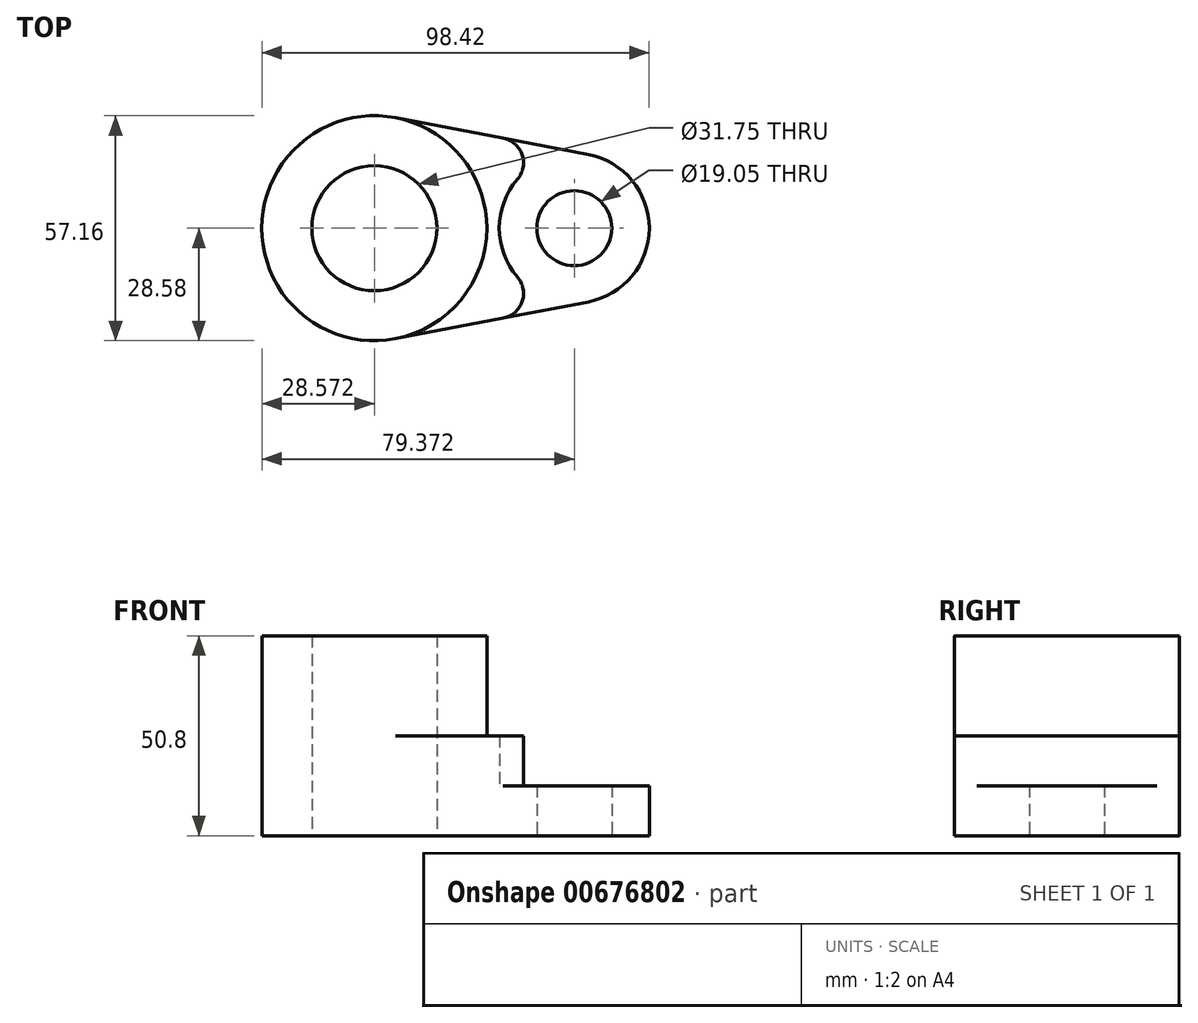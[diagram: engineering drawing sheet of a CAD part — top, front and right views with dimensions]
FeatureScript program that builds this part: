
annotation { "Feature Type Name" : "Feature", "Feature Type Description" : "" }
export const myFeature = defineFeature(function(context is Context, id is Id, definition is map)
    precondition{}
    {
        {
            var Q0;
            Q0=qCreatedBy(makeId("Top.planeOp"),FACE);
            var sketch = newSketch(context, id + "F0", { "sketchPlane" : qUnion([Q0])});
            skCircle(sketch, "E0", {"center": v(-26.89, 0) * mm, "radius": 28.58 * mm});
            skCircle(sketch, "E1", {"center": v(-26.89, 0) * mm, "radius": 15.88 * mm});
            skCircle(sketch, "E2", {"center": v(23.91, 0) * mm, "radius": 9.53 * mm});
            skCircle(sketch, "E3", {"center": v(23.91, 0) * mm, "radius": 19.05 * mm});
            skLineSegment(sketch, "E4", {"start": v(27.48, 18.71) * mm, "end": v(-21.53, 28.07) * mm});
            skLineSegment(sketch, "E5", {"start": v(27.48, -18.71) * mm, "end": v(-21.53, -28.07) * mm});
            skSolve(sketch);
        }
        {
            var Q0;
            Q0=makeQuery(id+"F0.imprint","IMPRINT",FACE,{"disambiguationData":[TD([[makeQuery(id+"F0.imprint","IMPRINT",EDGE,{"derivedFrom":sQuery(id+"F0.wireOp",EDGE,"E1")}),-1.0]])]});
            extrude(context, id + "F1", {"entities" : qUnion([Q0]), "depth" : 50.8 * mm, "offsetDistance" : 25.4 * mm});
        }
        {
            var Q0;
            {var subQ0=sQuery(id+"F0.wireOp",EDGE,"E4");Q0=makeQuery(id+"F0.imprint","IMPRINT",FACE,{"disambiguationData":[TD([[makeQuery(id+"F0.imprint","IMPRINT",EDGE,{"derivedFrom":subQ0}),1.0]])]});}
            extrude(context, id + "F2", {"entities" : qUnion([Q0]), "operationType" : NewBodyOperationType.ADD, "depth" : 25.4 * mm, "offsetDistance" : 25.4 * mm});
        }
        {
            var Q0;
            Q0=makeQuery(id+"F0.imprint","IMPRINT",FACE,{"disambiguationData":[TD([[makeQuery(id+"F0.imprint","IMPRINT",EDGE,{"derivedFrom":sQuery(id+"F0.wireOp",EDGE,"E2")}),-1.0]])]});
            extrude(context, id + "F3", {"entities" : qUnion([Q0]), "operationType" : NewBodyOperationType.ADD, "depth" : 12.7 * mm, "offsetDistance" : 25.4 * mm});
        }
        {
            var Q0;
            {var subQ0=sQuery(id+"F0.wireOp",EDGE,"E3");var subQ1=sQuery(id+"F0.wireOp",EDGE,"E5");Q0=makeQuery(id+"F3.boolean.opBoolean","SPLIT",EDGE,{"disambiguationData":[topologyDisambiguationEdgeConnected([makeQuery(id+"F2.opExtrude","SWEPT_FACE",FACE,{"disambiguationData":[OSD([subQ0])]})])],"derivedFrom":makeQuery(id+"F2.opExtrude","SWEPT_EDGE",EDGE,{"disambiguationData":[OSD([subQ0,subQ1])]})});}
            var Q1;
            {var subQ0=sQuery(id+"F0.wireOp",EDGE,"E3");var subQ1=sQuery(id+"F0.wireOp",EDGE,"E4");Q1=makeQuery(id+"F3.boolean.opBoolean","SPLIT",EDGE,{"disambiguationData":[topologyDisambiguationEdgeConnected([makeQuery(id+"F2.opExtrude","SWEPT_FACE",FACE,{"disambiguationData":[OSD([subQ0])]})])],"derivedFrom":makeQuery(id+"F2.opExtrude","SWEPT_EDGE",EDGE,{"disambiguationData":[OSD([subQ0,subQ1])]})});}
            fillet(context, id + "F4", {"entities" : qUnion([Q0, Q1]), "radius" : 6.35 * mm, "tangentPropagation" : true, "allowEdgeOverflow" : false});
        }
    });
